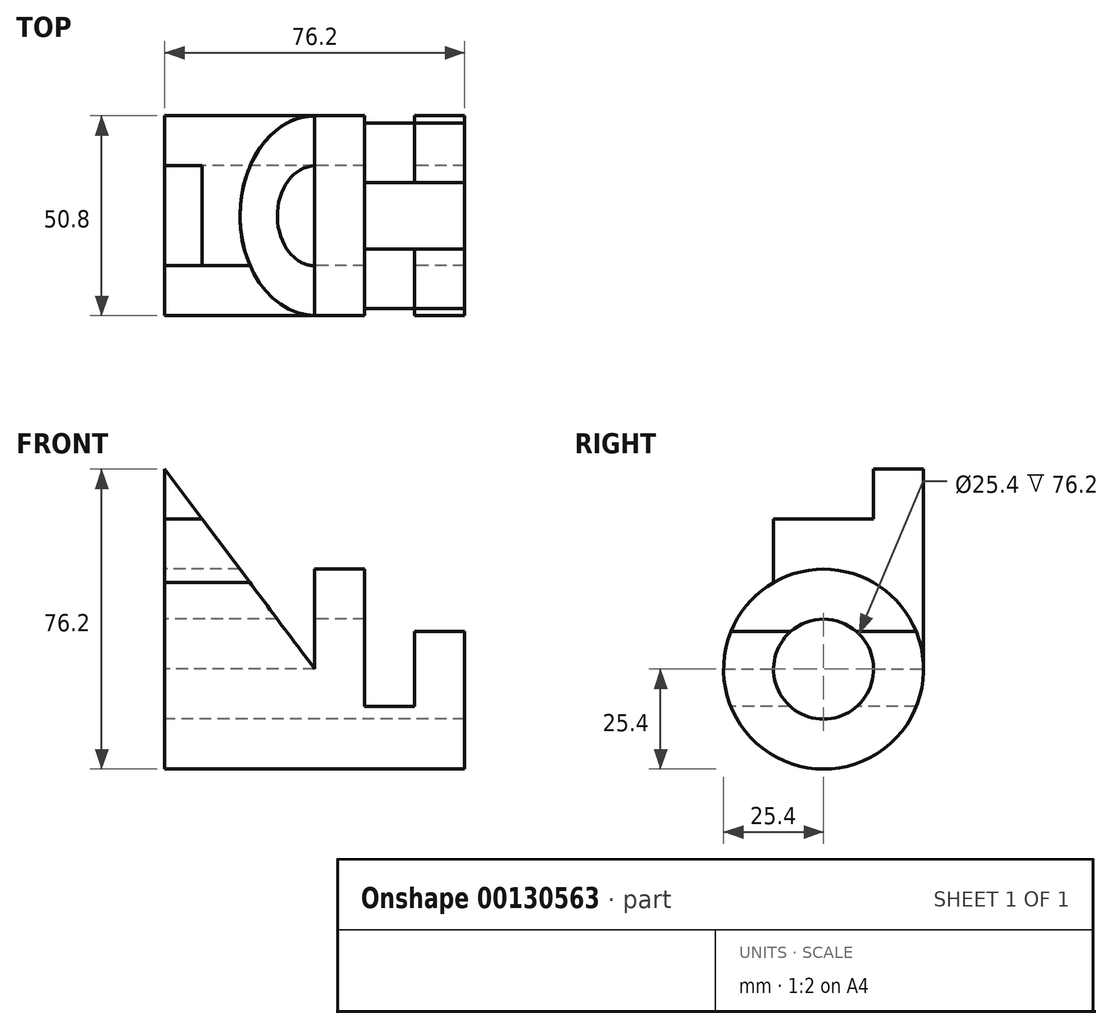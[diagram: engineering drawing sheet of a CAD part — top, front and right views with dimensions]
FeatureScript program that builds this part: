
annotation { "Feature Type Name" : "Feature", "Feature Type Description" : "" }
export const myFeature = defineFeature(function(context is Context, id is Id, definition is map)
    precondition{}
    {
        {
            var Q0;
            Q0=qCreatedBy(makeId("Right.planeOp"),FACE);
            var sketch = newSketch(context, id + "F0", { "sketchPlane" : qUnion([Q0])});
            skCircle(sketch, "E0", {"center": v(0, 0) * mm, "radius": 12.7 * mm});
            skCircle(sketch, "E1", {"center": v(0, 0) * mm, "radius": 25.4 * mm});
            skSolve(sketch);
        }
        {
            var Q0;
            Q0 = qSketchRegion(id + "F0", true);
            extrude(context, id + "F1", {"entities" : qUnion([Q0]), "depth" : 76.2 * mm});
        }
        {
            var Q0;
            Q0=makeQuery(id+"F1.opExtrude","CAP_FACE",FACE,{"disambiguationData":[OSD([sQuery(id+"F0.wireOp",EDGE,"E0"),sQuery(id+"F0.wireOp",EDGE,"E1")])],"isStart":true});
            var sketch = newSketch(context, id + "F2", { "sketchPlane" : qUnion([Q0])});
            skLineSegment(sketch, "E2", {"start": v(-25.4, 0) * mm, "end": v(-25.4, 50.8) * mm});
            skLineSegment(sketch, "E3", {"start": v(-25.4, 50.8) * mm, "end": v(-12.7, 50.8) * mm});
            skLineSegment(sketch, "E4", {"start": v(-12.7, 50.8) * mm, "end": v(-12.7, 38.1) * mm});
            skLineSegment(sketch, "E5", {"start": v(-12.7, 38.1) * mm, "end": v(12.7, 38.1) * mm});
            skLineSegment(sketch, "E6", {"start": v(12.7, 38.1) * mm, "end": v(12.7, 22) * mm});
            skSolve(sketch);
        }
        {
            var Q0;
            Q0 = qSketchRegion(id + "F2", true);
            var Q1;
            {var subQ0=sQuery(id+"F2.wireOp",EDGE,"E2");Q1=makeQuery(id+"F2.imprint","IMPRINT",FACE,{"disambiguationData":[TD([[makeQuery(id+"F2.imprint","IMPRINT",EDGE,{"derivedFrom":subQ0}),-1.0]])]});}
            extrude(context, id + "F3", {"entities" : qUnion([Q0, Q1]), "oppositeDirection" : true, "depth" : 38.1 * mm});
        }
        {
            var Q0;
            Q0=makeQuery(id+"F3.opExtrude","SWEPT_FACE",FACE,{"disambiguationData":[OSD([sQuery(id+"F2.wireOp",EDGE,"E2")])]});
            var sketch = newSketch(context, id + "F4", { "sketchPlane" : qUnion([Q0])});
            skLineSegment(sketch, "E7", {"start": v(-38.1, 0) * mm, "end": v(0, 50.8) * mm});
            skLineSegment(sketch, "E8", {"start": v(0, 50.8) * mm, "end": v(-38.1, 50.8) * mm});
            skLineSegment(sketch, "E9", {"start": v(-38.1, 50.8) * mm, "end": v(-38.1, 0) * mm});
            skSolve(sketch);
        }
        {
            var Q0;
            Q0 = qSketchRegion(id + "F4", true);
            extrude(context, id + "F5", {"entities" : qUnion([Q0]), "operationType" : NewBodyOperationType.REMOVE, "endBound" : BoundingType.THROUGH_ALL, "oppositeDirection" : true, "depth" : 25.4 * mm});
        }
        {
            var Q0;
            Q0=qCreatedBy(makeId("Front.planeOp"),FACE);
            var sketch = newSketch(context, id + "F6", { "sketchPlane" : qUnion([Q0])});
            skLineSegment(sketch, "E10", {"start": v(0, 0) * mm, "end": v(0, 25.4) * mm, "construction": true});
            skLineSegment(sketch, "E11", {"start": v(0, 25.4) * mm, "end": v(76.2, 25.4) * mm, "construction": true});
            skLineSegment(sketch, "E12", {"start": v(76.2, 25.4) * mm, "end": v(76.2, 9.53) * mm});
            skLineSegment(sketch, "E13", {"start": v(76.2, 9.53) * mm, "end": v(63.5, 9.53) * mm});
            skLineSegment(sketch, "E14", {"start": v(63.5, 9.53) * mm, "end": v(63.5, -9.52) * mm});
            skLineSegment(sketch, "E15", {"start": v(63.5, -9.52) * mm, "end": v(50.8, -9.52) * mm});
            skLineSegment(sketch, "E16", {"start": v(50.8, -9.53) * mm, "end": v(50.8, 25.4) * mm});
            skLineSegment(sketch, "E17", {"start": v(50.8, 25.4) * mm, "end": v(76.2, 25.4) * mm});
            skSolve(sketch);
        }
        {
            var Q0;
            Q0 = qSketchRegion(id + "F6", true);
            extrude(context, id + "F7", {"entities" : qUnion([Q0]), "operationType" : NewBodyOperationType.REMOVE, "endBound" : BoundingType.THROUGH_ALL, "oppositeDirection" : true, "depth" : 25.4 * mm, "hasSecondDirection" : true, "secondDirectionBound" : SecondDirectionBoundingType.THROUGH_ALL, "secondDirectionOppositeDirection" : false, "secondDirectionDepth" : 25.4 * mm});
        }
    });
